# Revit family: 1Electronics_Commercial-Audio_Biamp_Microphone-Discussion-System_MDS-Chair_MDS-Del
name_source: partatom
category: Communication Devices
units: mm (PartAtom-declared; Revit-internal decimal feet)

## family parameters
Cut with Voids When Loaded = No
Host = Face
Maintain Annotation Orientation = No
OmniClass Number = 23.85.10.11.14.14.11
Part Type = Normal
Room Calculation Point = No
Round Connector Dimension = Use Diameter
Shared = No

## types (2) — shared parameters
Apparent Load = 0 VA
Connector Description = DC IN15V
Default Elevation = 4' - 0"
Depth = 0' - 6 1/2"
Frequency response = 80 Hz - 16 kHz
Height = 0' - 2"
Housing Material = Biamp - Plastic - Dark Gray
Manufacturer = Biamp
Max Power Consumption = 0 W
Maximum SPL = 100 dB for 1% THD
Microphone type = Unidirectional condensor
Number of Poles = 1
Power Factor = 1
Product Documentation Link = https://downloads.biamp.com
Product Page URL = https://www.biamp.com
Product data url = https://www.bimobject.com
System interconnection = RJ45 - CAT5 cables, straight, according to EIA-568-B
URL = https://www.biamp.com
Voltage = 15 V
Weight = 1.61 lb
Width = 0' - 4 1/2"

## per-type parameters (varying)
| type | Accessories supplied | CHAIR | DEL | Description |
| MDS Chair | Manual, microphone foam cap | Yes | No | MDS.CHAIR Chairman Microphone for Microphone Discussion System |
| MCS Del |  | No | Yes | MDS.DEL Delegate Microphone for Microphone Discussion System |

note: column(s) folded — value = type name in every type: Model

## geometry (parser evidence)
native form markers: Sweep x2
no freeform markers — native parametric forms only
